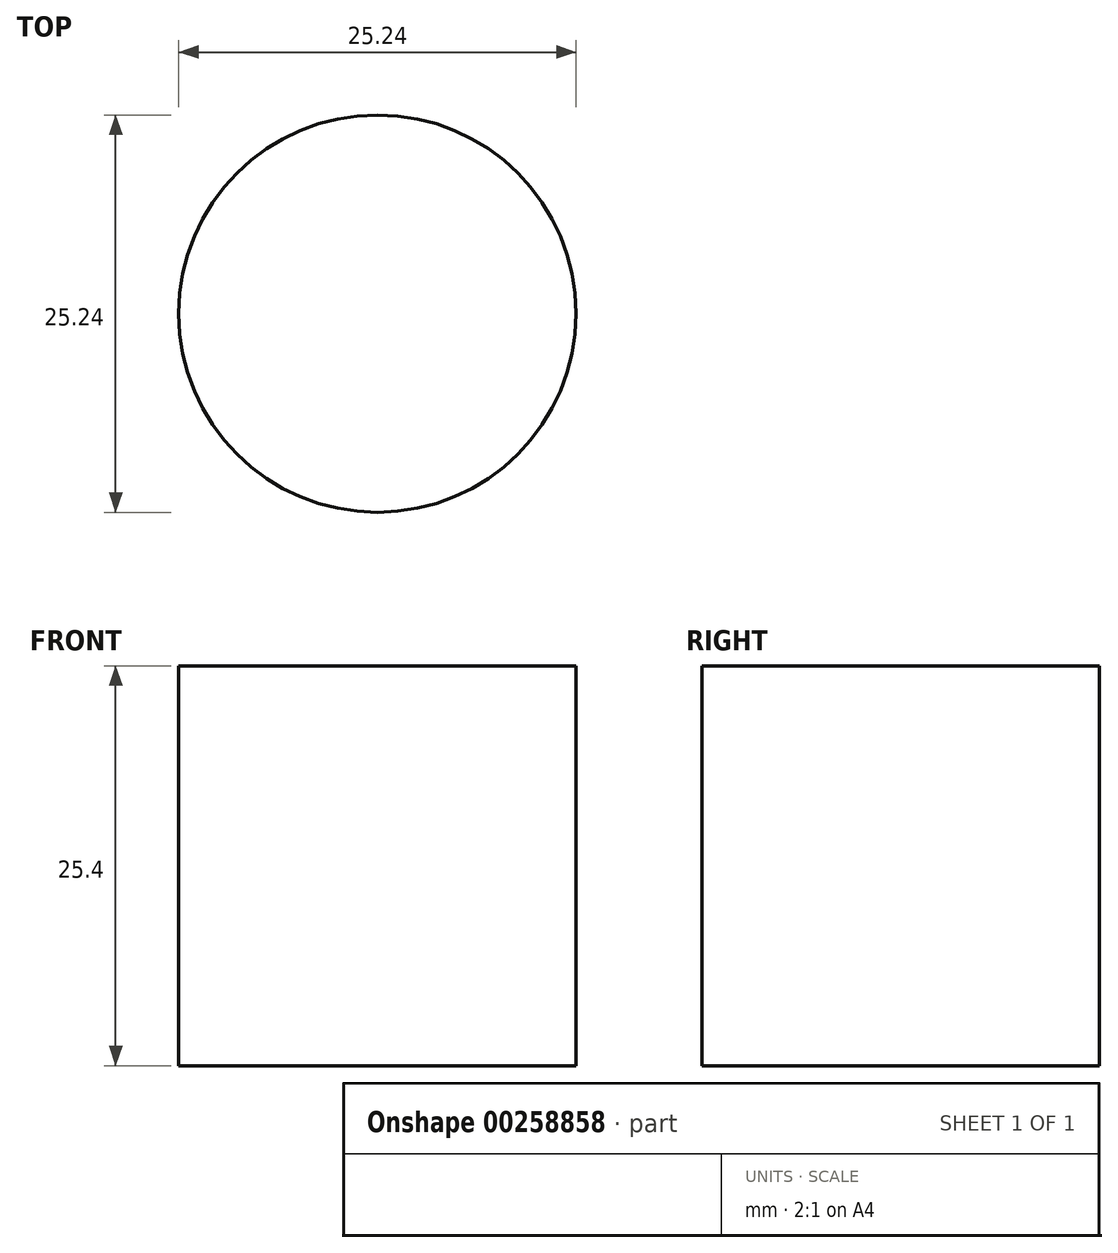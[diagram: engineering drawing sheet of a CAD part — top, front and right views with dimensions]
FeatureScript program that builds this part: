
annotation { "Feature Type Name" : "Feature", "Feature Type Description" : "" }
export const myFeature = defineFeature(function(context is Context, id is Id, definition is map)
    precondition{}
    {
        {
            var Q0;
            Q0=qCreatedBy(makeId("Top.planeOp"),FACE);
            var sketch = newSketch(context, id + "F0", { "sketchPlane" : qUnion([Q0])});
            skCircle(sketch, "E0", {"center": v(0, 0) * mm, "radius": 12.62 * mm});
            skSolve(sketch);
        }
        {
            var Q0;
            Q0=makeQuery(id+"F0.imprint","IMPRINT",FACE,{"disambiguationData":[TD([[makeQuery(id+"F0.imprint","IMPRINT",EDGE,{"derivedFrom":sQuery(id+"F0.wireOp",EDGE,"E0")}),1.0]])]});
            extrude(context, id + "F1", {"entities" : qUnion([Q0]), "depth" : 25.4 * mm});
        }
    });
